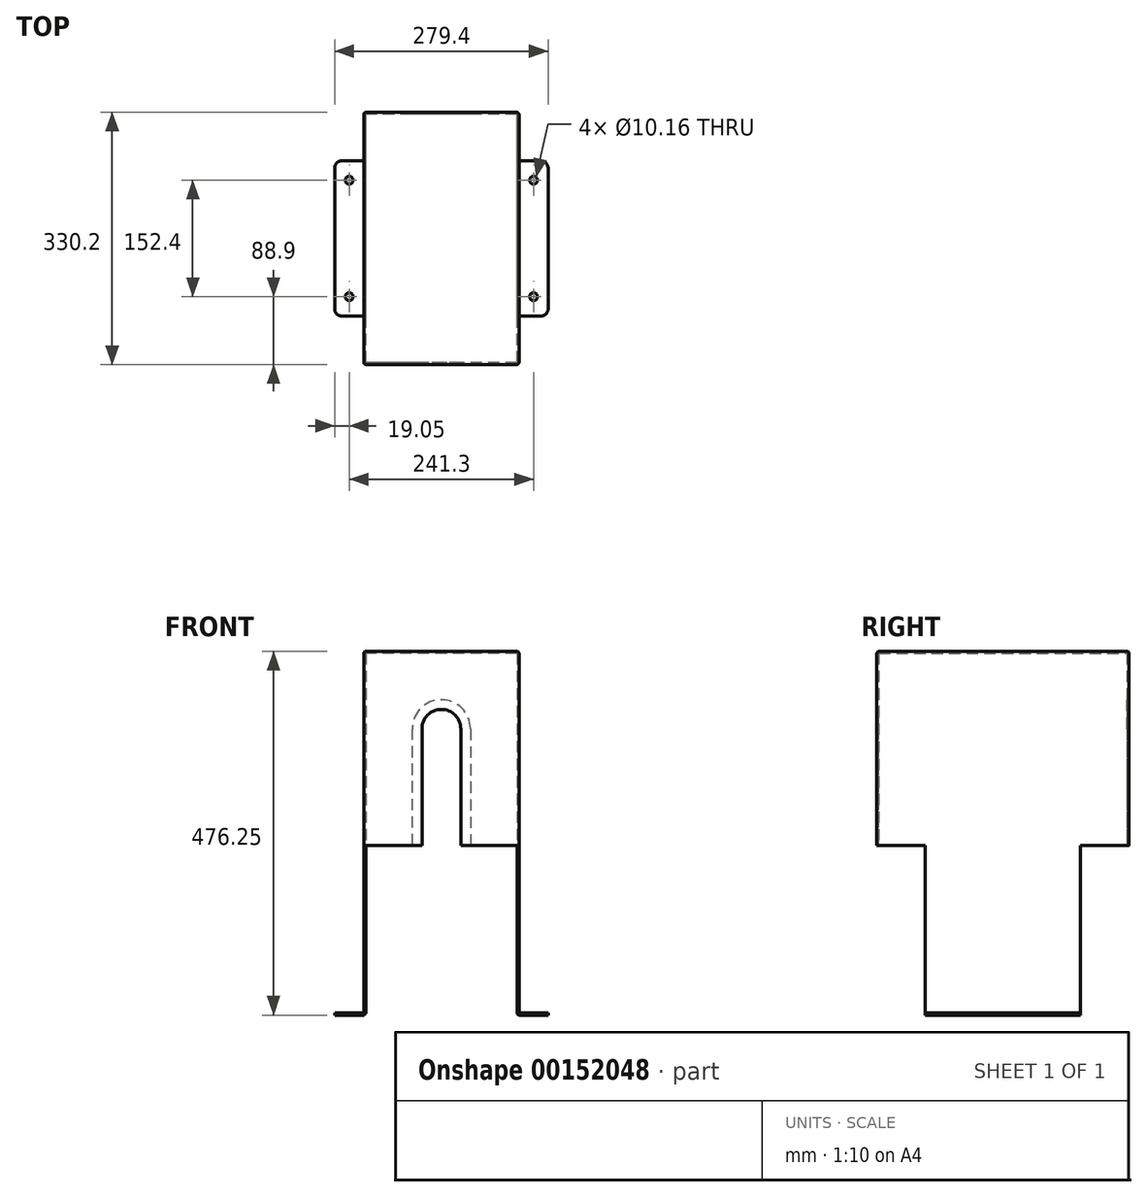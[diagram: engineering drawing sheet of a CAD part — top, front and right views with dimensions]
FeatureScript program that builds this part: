
annotation { "Feature Type Name" : "Feature", "Feature Type Description" : "" }
export const myFeature = defineFeature(function(context is Context, id is Id, definition is map)
    precondition{}
    {
        {
            var Q0;
            Q0=qCreatedBy(makeId("Top.planeOp"),FACE);
            var sketch = newSketch(context, id + "F0", { "sketchPlane" : qUnion([Q0])});
            skLineSegment(sketch, "E0.bottom", {"start": v(101.6, -165.1) * mm, "end": v(-101.6, -165.1) * mm});
            skLineSegment(sketch, "E0.top", {"start": v(101.6, 165.1) * mm, "end": v(-101.6, 165.1) * mm});
            skLineSegment(sketch, "E0.left", {"start": v(101.6, -165.1) * mm, "end": v(101.6, 165.1) * mm});
            skLineSegment(sketch, "E0.right", {"start": v(-101.6, -165.1) * mm, "end": v(-101.6, 165.1) * mm});
            skPoint(sketch, "E0.middle", {"position": v(0, 0) * mm});
            skSolve(sketch);
        }
        {
            var Q0;
            Q0 = qSketchRegion(id + "F0", true);
            extrude(context, id + "F1", {"entities" : qUnion([Q0]), "depth" : 254 * mm});
        }
        {
            var Q0;
            Q0=makeQuery(id+"F1.opExtrude","CAP_FACE",FACE,{"disambiguationData":[OSD([sQuery(id+"F0.wireOp",EDGE,"E0.bottom"),sQuery(id+"F0.wireOp",EDGE,"E0.top"),sQuery(id+"F0.wireOp",EDGE,"E0.left"),sQuery(id+"F0.wireOp",EDGE,"E0.right")])],"isStart":true});
            shell(context, id + "F2", {"entities" : qUnion([Q0]), "thickness" : 2.54 * mm});
        }
        {
            var Q0;
            Q0=makeQuery(id+"F1.opExtrude","SWEPT_FACE",FACE,{"disambiguationData":[OSD([sQuery(id+"F0.wireOp",EDGE,"E0.bottom")])]});
            var sketch = newSketch(context, id + "F3", { "sketchPlane" : qUnion([Q0])});
            skLineSegment(sketch, "E1", {"start": v(0, 0) * mm, "end": v(0, 152.4) * mm});
            skCircle(sketch, "E2", {"center": v(0, 152.4) * mm, "radius": 25.4 * mm});
            skLineSegment(sketch, "E3", {"start": v(0, 0) * mm, "end": v(-25.4, 0) * mm});
            skLineSegment(sketch, "E4", {"start": v(-25.4, 0) * mm, "end": v(-25.4, 152.4) * mm});
            skLineSegment(sketch, "E5", {"start": v(-25.4, 152.4) * mm, "end": v(25.4, 152.4) * mm});
            skLineSegment(sketch, "E6", {"start": v(25.4, 152.4) * mm, "end": v(25.4, 0) * mm});
            skLineSegment(sketch, "E7", {"start": v(25.4, 0) * mm, "end": v(0, 0) * mm});
            skSolve(sketch);
        }
        {
            var Q0;
            Q0 = qSketchRegion(id + "F3", true);
            extrude(context, id + "F4", {"entities" : qUnion([Q0]), "operationType" : NewBodyOperationType.REMOVE, "oppositeDirection" : true, "depth" : 25.4 * mm});
        }
        {
            var Q0;
            Q0=makeQuery(id+"F1.opExtrude","SWEPT_FACE",FACE,{"disambiguationData":[OSD([sQuery(id+"F0.wireOp",EDGE,"E0.top")])]});
            var sketch = newSketch(context, id + "F5", { "sketchPlane" : qUnion([Q0])});
            skLineSegment(sketch, "E8", {"start": v(0, 0) * mm, "end": v(0, 152.4) * mm});
            skCircle(sketch, "E9", {"center": v(0, 152.4) * mm, "radius": 38.1 * mm});
            skLineSegment(sketch, "E10", {"start": v(0, 0) * mm, "end": v(-38.1, 0) * mm});
            skLineSegment(sketch, "E11", {"start": v(-38.1, 0) * mm, "end": v(-38.1, 152.4) * mm});
            skLineSegment(sketch, "E12", {"start": v(-38.1, 152.4) * mm, "end": v(38.1, 152.4) * mm});
            skLineSegment(sketch, "E13", {"start": v(38.1, 152.4) * mm, "end": v(38.1, 0) * mm});
            skLineSegment(sketch, "E14", {"start": v(38.1, 0) * mm, "end": v(0, 0) * mm});
            skSolve(sketch);
        }
        {
            var Q0;
            Q0 = qSketchRegion(id + "F5", true);
            extrude(context, id + "F6", {"entities" : qUnion([Q0]), "operationType" : NewBodyOperationType.REMOVE, "oppositeDirection" : true, "depth" : 25.4 * mm});
        }
        {
            var Q0;
            {var subQ0=sQuery(id+"F0.wireOp",EDGE,"E0.bottom");var subQ1=sQuery(id+"F0.wireOp",EDGE,"E0.left");var subQ2=sQuery(id+"F0.wireOp",EDGE,"E0.top");Q0=makeQuery(id+"F6.boolean.opBoolean","SPLIT",FACE,{"disambiguationData":[TD([makeQuery(id+"F1.opExtrude","SWEPT_FACE",FACE,{"disambiguationData":[OSD([subQ1])]})])],"derivedFrom":makeQuery(id+"F1.opExtrude","CAP_FACE",FACE,{"disambiguationData":[OSD([subQ0,subQ2,subQ1,sQuery(id+"F0.wireOp",EDGE,"E0.right")])],"isStart":true})});}
            var sketch = newSketch(context, id + "F7", { "sketchPlane" : qUnion([Q0])});
            skLineSegment(sketch, "E15", {"start": v(99.06, 0) * mm, "end": v(99.06, -101.6) * mm});
            skLineSegment(sketch, "E16", {"start": v(99.06, -101.6) * mm, "end": v(101.6, -101.6) * mm});
            skLineSegment(sketch, "E17", {"start": v(101.6, -101.6) * mm, "end": v(101.6, 101.6) * mm});
            skLineSegment(sketch, "E18", {"start": v(101.6, 101.6) * mm, "end": v(99.06, 101.6) * mm});
            skLineSegment(sketch, "E19", {"start": v(99.06, 101.6) * mm, "end": v(99.06, 0) * mm});
            skSolve(sketch);
        }
        {
            var Q0;
            Q0 = qSketchRegion(id + "F7", true);
            extrude(context, id + "F8", {"entities" : qUnion([Q0]), "operationType" : NewBodyOperationType.ADD, "depth" : 222.25 * mm});
        }
        {
            var Q0;
            {var subQ0=sQuery(id+"F0.wireOp",EDGE,"E0.bottom");var subQ1=sQuery(id+"F0.wireOp",EDGE,"E0.right");var subQ2=sQuery(id+"F0.wireOp",EDGE,"E0.top");Q0=makeQuery(id+"F6.boolean.opBoolean","SPLIT",FACE,{"disambiguationData":[TD([makeQuery(id+"F1.opExtrude","SWEPT_FACE",FACE,{"disambiguationData":[OSD([subQ1])]})])],"derivedFrom":makeQuery(id+"F1.opExtrude","CAP_FACE",FACE,{"disambiguationData":[OSD([subQ0,subQ2,sQuery(id+"F0.wireOp",EDGE,"E0.left"),subQ1])],"isStart":true})});}
            var sketch = newSketch(context, id + "F9", { "sketchPlane" : qUnion([Q0])});
            skLineSegment(sketch, "E20", {"start": v(-99.06, 0) * mm, "end": v(-99.06, -101.6) * mm});
            skLineSegment(sketch, "E21", {"start": v(-99.06, -101.6) * mm, "end": v(-101.6, -101.6) * mm});
            skLineSegment(sketch, "E22", {"start": v(-101.6, -101.6) * mm, "end": v(-101.6, 101.6) * mm});
            skLineSegment(sketch, "E23", {"start": v(-101.6, 101.6) * mm, "end": v(-99.06, 101.6) * mm});
            skLineSegment(sketch, "E24", {"start": v(-99.06, 101.6) * mm, "end": v(-99.06, 0) * mm});
            skSolve(sketch);
        }
        {
            var Q0;
            Q0 = qSketchRegion(id + "F9", true);
            extrude(context, id + "F10", {"entities" : qUnion([Q0]), "operationType" : NewBodyOperationType.ADD, "depth" : 222.25 * mm});
        }
        {
            var Q0;
            Q0=makeQuery(id+"F8.boolean.opBoolean","MERGE",FACE,{"derivedFrom":[makeQuery(id+"F1.opExtrude","SWEPT_FACE",FACE,{"disambiguationData":[OSD([sQuery(id+"F0.wireOp",EDGE,"E0.left")])]}),makeQuery(id+"F8.opExtrude","SWEPT_FACE",FACE,{"disambiguationData":[OSD([sQuery(id+"F7.wireOp",EDGE,"E17")])]})]});
            var sketch = newSketch(context, id + "F11", { "sketchPlane" : qUnion([Q0])});
            skLineSegment(sketch, "E25.bottom", {"start": v(101.6, -222.25) * mm, "end": v(-101.6, -222.25) * mm});
            skLineSegment(sketch, "E25.top", {"start": v(101.6, -219.08) * mm, "end": v(-101.6, -219.08) * mm});
            skLineSegment(sketch, "E25.left", {"start": v(101.6, -222.25) * mm, "end": v(101.6, -219.08) * mm});
            skLineSegment(sketch, "E25.right", {"start": v(-101.6, -222.25) * mm, "end": v(-101.6, -219.08) * mm});
            skSolve(sketch);
        }
        {
            var Q0;
            Q0 = qSketchRegion(id + "F11", true);
            extrude(context, id + "F12", {"entities" : qUnion([Q0]), "operationType" : NewBodyOperationType.ADD, "depth" : 38.1 * mm});
        }
        {
            var Q0;
            Q0=makeQuery(id+"F10.boolean.opBoolean","MERGE",FACE,{"derivedFrom":[makeQuery(id+"F1.opExtrude","SWEPT_FACE",FACE,{"disambiguationData":[OSD([sQuery(id+"F0.wireOp",EDGE,"E0.right")])]}),makeQuery(id+"F10.opExtrude","SWEPT_FACE",FACE,{"disambiguationData":[OSD([sQuery(id+"F9.wireOp",EDGE,"E22")])]})]});
            var sketch = newSketch(context, id + "F13", { "sketchPlane" : qUnion([Q0])});
            skLineSegment(sketch, "E26.bottom", {"start": v(-101.6, -222.25) * mm, "end": v(101.6, -222.25) * mm});
            skLineSegment(sketch, "E26.top", {"start": v(-101.6, -219.08) * mm, "end": v(101.6, -219.08) * mm});
            skLineSegment(sketch, "E26.left", {"start": v(-101.6, -222.25) * mm, "end": v(-101.6, -219.08) * mm});
            skLineSegment(sketch, "E26.right", {"start": v(101.6, -222.25) * mm, "end": v(101.6, -219.08) * mm});
            skSolve(sketch);
        }
        {
            var Q0;
            Q0 = qSketchRegion(id + "F13", true);
            extrude(context, id + "F14", {"entities" : qUnion([Q0]), "operationType" : NewBodyOperationType.ADD, "depth" : 38.1 * mm});
        }
        {
            var Q0;
            Q0=makeQuery(id+"F12.boolean.opBoolean","MERGE",FACE,{"derivedFrom":[makeQuery(id+"F8.opExtrude","CAP_FACE",FACE,{"disambiguationData":[OSD([sQuery(id+"F7.wireOp",EDGE,"E15"),sQuery(id+"F7.wireOp",EDGE,"E16"),sQuery(id+"F7.wireOp",EDGE,"E17"),sQuery(id+"F7.wireOp",EDGE,"E18"),sQuery(id+"F7.wireOp",EDGE,"E19")])],"isStart":false}),makeQuery(id+"F12.opExtrude","SWEPT_FACE",FACE,{"disambiguationData":[OSD([sQuery(id+"F11.wireOp",EDGE,"E25.bottom")])]})]});
            var sketch = newSketch(context, id + "F15", { "sketchPlane" : qUnion([Q0])});
            skPoint(sketch, "E27.middle", {"position": v(0, 0) * mm});
            skCircle(sketch, "E28", {"center": v(120.65, 76.2) * mm, "radius": 5.08 * mm});
            skCircle(sketch, "E29", {"center": v(120.65, -76.2) * mm, "radius": 5.08 * mm});
            skCircle(sketch, "E30", {"center": v(-120.65, 76.2) * mm, "radius": 5.08 * mm});
            skCircle(sketch, "E31", {"center": v(-120.65, -76.2) * mm, "radius": 5.08 * mm});
            skSolve(sketch);
        }
        {
            var Q0;
            Q0 = qSketchRegion(id + "F15", true);
            extrude(context, id + "F16", {"entities" : qUnion([Q0]), "operationType" : NewBodyOperationType.REMOVE, "oppositeDirection" : true, "depth" : 25.4 * mm});
        }
        {
            var Q0;
            Q0=makeQuery(id+"F12.opExtrude","CAP_EDGE",EDGE,{"disambiguationData":[OSD([sQuery(id+"F11.wireOp",EDGE,"E25.top")])],"isStart":true});
            var Q1;
            Q1=makeQuery(id+"F8.opExtrude","CAP_EDGE",EDGE,{"disambiguationData":[OSD([sQuery(id+"F7.wireOp",EDGE,"E15"),sQuery(id+"F7.wireOp",EDGE,"E19")])],"isStart":false});
            var Q2;
            Q2=makeQuery(id+"F10.opExtrude","CAP_EDGE",EDGE,{"disambiguationData":[OSD([sQuery(id+"F9.wireOp",EDGE,"E20"),sQuery(id+"F9.wireOp",EDGE,"E24")])],"isStart":false});
            var Q3;
            Q3=makeQuery(id+"F14.opExtrude","CAP_EDGE",EDGE,{"disambiguationData":[OSD([sQuery(id+"F13.wireOp",EDGE,"E26.top")])],"isStart":true});
            var Q4;
            Q4=makeQuery(id+"F1.opExtrude","SWEPT_EDGE",EDGE,{"disambiguationData":[OSD([sQuery(id+"F0.wireOp",EDGE,"E0.bottom"),sQuery(id+"F0.wireOp",EDGE,"E0.right")])]});
            var Q5;
            Q5=makeQuery(id+"F1.opExtrude","CAP_EDGE",EDGE,{"disambiguationData":[OSD([sQuery(id+"F0.wireOp",EDGE,"E0.bottom")])],"isStart":false});
            var Q6;
            Q6=makeQuery(id+"F1.opExtrude","SWEPT_EDGE",EDGE,{"disambiguationData":[OSD([sQuery(id+"F0.wireOp",EDGE,"E0.bottom"),sQuery(id+"F0.wireOp",EDGE,"E0.left")])]});
            var Q7;
            Q7=makeQuery(id+"F1.opExtrude","SWEPT_EDGE",EDGE,{"disambiguationData":[OSD([sQuery(id+"F0.wireOp",EDGE,"E0.top"),sQuery(id+"F0.wireOp",EDGE,"E0.right")])]});
            var Q8;
            Q8=makeQuery(id+"F1.opExtrude","CAP_EDGE",EDGE,{"disambiguationData":[OSD([sQuery(id+"F0.wireOp",EDGE,"E0.top")])],"isStart":false});
            var Q9;
            Q9=makeQuery(id+"F1.opExtrude","SWEPT_EDGE",EDGE,{"disambiguationData":[OSD([sQuery(id+"F0.wireOp",EDGE,"E0.top"),sQuery(id+"F0.wireOp",EDGE,"E0.left")])]});
            var Q10;
            Q10=makeQuery(id+"F1.opExtrude","CAP_EDGE",EDGE,{"disambiguationData":[OSD([sQuery(id+"F0.wireOp",EDGE,"E0.right")])],"isStart":false});
            var Q11;
            Q11=makeQuery(id+"F1.opExtrude","CAP_EDGE",EDGE,{"disambiguationData":[OSD([sQuery(id+"F0.wireOp",EDGE,"E0.left")])],"isStart":false});
            fillet(context, id + "F17", {"entities" : qUnion([Q0, Q1, Q2, Q3, Q4, Q5, Q6, Q7, Q8, Q9, Q10, Q11]), "radius" : 3.17 * mm, "tangentPropagation" : true, "allowEdgeOverflow" : false});
        }
        {
            var Q0;
            Q0=makeQuery(id+"F14.opExtrude","CAP_EDGE",EDGE,{"disambiguationData":[OSD([sQuery(id+"F13.wireOp",EDGE,"E26.left")])],"isStart":false});
            var Q1;
            Q1=makeQuery(id+"F14.opExtrude","CAP_EDGE",EDGE,{"disambiguationData":[OSD([sQuery(id+"F13.wireOp",EDGE,"E26.right")])],"isStart":false});
            var Q2;
            Q2=makeQuery(id+"F12.opExtrude","CAP_EDGE",EDGE,{"disambiguationData":[OSD([sQuery(id+"F11.wireOp",EDGE,"E25.right")])],"isStart":false});
            var Q3;
            Q3=makeQuery(id+"F12.opExtrude","CAP_EDGE",EDGE,{"disambiguationData":[OSD([sQuery(id+"F11.wireOp",EDGE,"E25.left")])],"isStart":false});
            fillet(context, id + "F18", {"entities" : qUnion([Q0, Q1, Q2, Q3]), "radius" : 9.52 * mm, "tangentPropagation" : true, "allowEdgeOverflow" : false});
        }
    });
